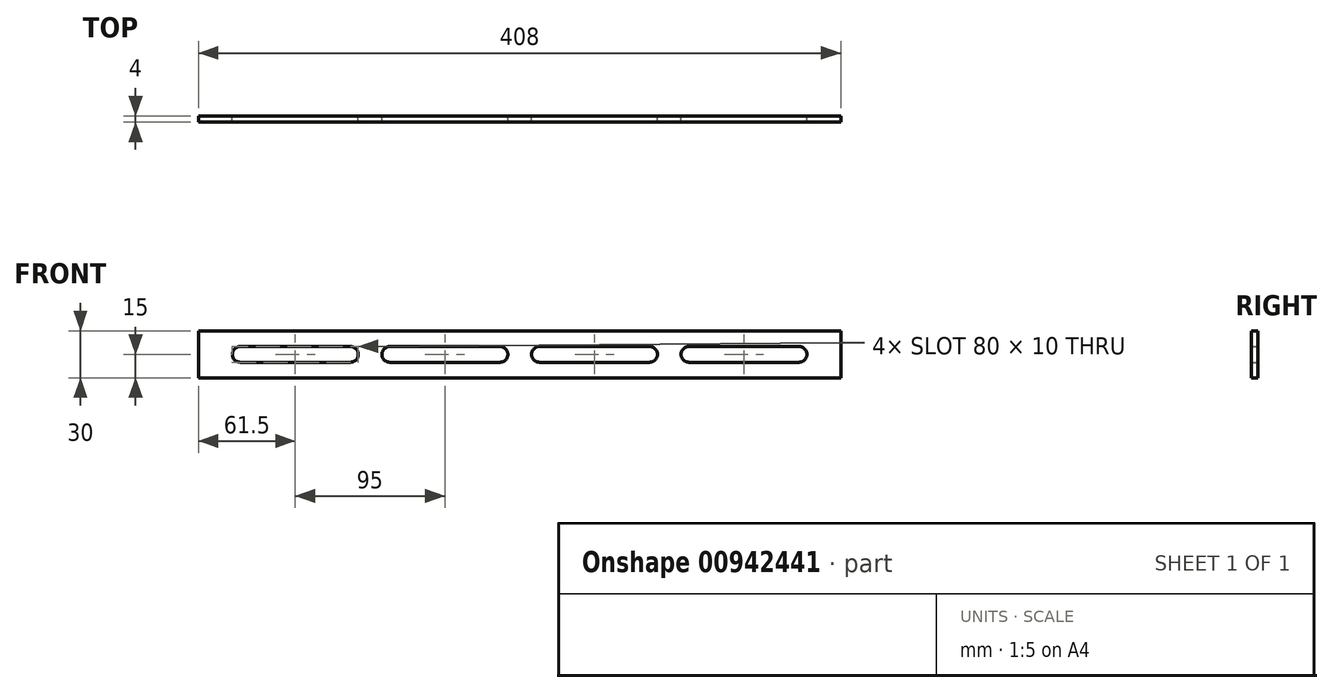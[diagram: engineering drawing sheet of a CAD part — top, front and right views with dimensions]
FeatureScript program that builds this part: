
annotation { "Feature Type Name" : "Feature", "Feature Type Description" : "" }
export const myFeature = defineFeature(function(context is Context, id is Id, definition is map)
    precondition{}
    {
        {
            var Q0;
            Q0=qCreatedBy(makeId("Front.planeOp"),FACE);
            var sketch = newSketch(context, id + "F0", { "sketchPlane" : qUnion([Q0])});
            skLineSegment(sketch, "E0.bottom", {"start": v(-204, 0) * mm, "end": v(204, 0) * mm});
            skLineSegment(sketch, "E0.top", {"start": v(-204, 30) * mm, "end": v(204, 30) * mm});
            skLineSegment(sketch, "E0.left", {"start": v(-204, 0) * mm, "end": v(-204, 30) * mm});
            skLineSegment(sketch, "E0.right", {"start": v(204, 0) * mm, "end": v(204, 30) * mm});
            skLineSegment(sketch, "E1.bottom", {"start": v(-177.5, 20) * mm, "end": v(-107.5, 20) * mm});
            skLineSegment(sketch, "E1.top", {"start": v(-177.5, 10) * mm, "end": v(-107.5, 10) * mm});
            skArc(sketch, "E2", {"start": v(-107.5, 10) * mm, "mid": v(-102.5, 15) * mm, "end": v(-107.5, 20) * mm});
            skArc(sketch, "E3", {"start": v(-177.5, 20) * mm, "mid": v(-182.5, 15) * mm, "end": v(-177.5, 10) * mm});
            skLineSegment(sketch, "E4.1.0.0", {"start": v(-82.5, 20) * mm, "end": v(-12.5, 20) * mm});
            skLineSegment(sketch, "E4.1.0.1", {"start": v(-82.5, 10) * mm, "end": v(-12.5, 10) * mm});
            skArc(sketch, "E4.1.0.2", {"start": v(-12.5, 10) * mm, "mid": v(-7.5, 15) * mm, "end": v(-12.5, 20) * mm});
            skArc(sketch, "E4.1.0.3", {"start": v(-82.5, 20) * mm, "mid": v(-87.5, 15) * mm, "end": v(-82.5, 10) * mm});
            skLineSegment(sketch, "E4.2.0.0", {"start": v(12.5, 20) * mm, "end": v(82.5, 20) * mm});
            skLineSegment(sketch, "E4.2.0.1", {"start": v(12.5, 10) * mm, "end": v(82.5, 10) * mm});
            skArc(sketch, "E4.2.0.2", {"start": v(82.5, 10) * mm, "mid": v(87.5, 15) * mm, "end": v(82.5, 20) * mm});
            skArc(sketch, "E4.2.0.3", {"start": v(12.5, 20) * mm, "mid": v(7.5, 15) * mm, "end": v(12.5, 10) * mm});
            skLineSegment(sketch, "E4.3.0.0", {"start": v(107.5, 20) * mm, "end": v(177.5, 20) * mm});
            skLineSegment(sketch, "E4.3.0.1", {"start": v(107.5, 10) * mm, "end": v(177.5, 10) * mm});
            skArc(sketch, "E4.3.0.2", {"start": v(177.5, 10) * mm, "mid": v(182.5, 15) * mm, "end": v(177.5, 20) * mm});
            skArc(sketch, "E4.3.0.3", {"start": v(107.5, 20) * mm, "mid": v(102.5, 15) * mm, "end": v(107.5, 10) * mm});
            skLineSegment(sketch, "E4.direction1", {"start": v(-177.5, 10) * mm, "end": v(-82.5, 10) * mm, "construction": true});
            skSolve(sketch);
        }
        {
            var Q0;
            Q0 = qSketchRegion(id + "F0", true);
            extrude(context, id + "F1", {"entities" : qUnion([Q0]), "depth" : 4 * mm, "offsetDistance" : 25 * mm});
        }
    });
